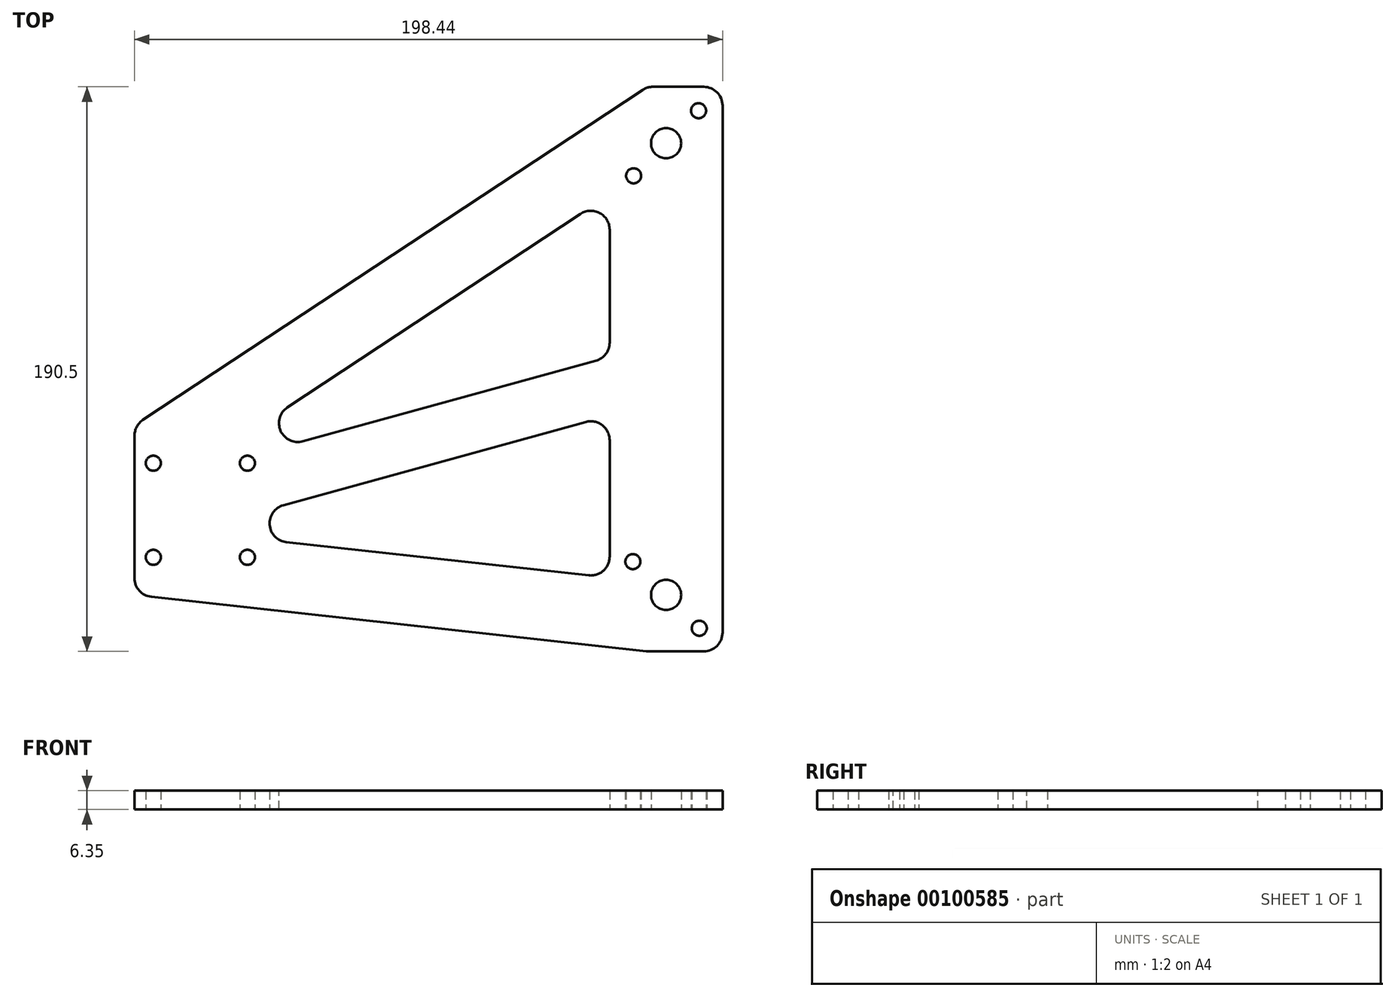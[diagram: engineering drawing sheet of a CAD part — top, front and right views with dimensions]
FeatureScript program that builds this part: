
annotation { "Feature Type Name" : "Feature", "Feature Type Description" : "" }
export const myFeature = defineFeature(function(context is Context, id is Id, definition is map)
    precondition{}
    {
        {
            var Q0;
            Q0=qCreatedBy(makeId("Top.planeOp"),FACE);
            var sketch = newSketch(context, id + "F0", { "sketchPlane" : qUnion([Q0])});
            skLineSegment(sketch, "E0.bottom", {"start": v(99.22, 127) * mm, "end": v(-99.22, 127) * mm});
            skLineSegment(sketch, "E0.top", {"start": v(99.22, -63.5) * mm, "end": v(-99.22, -63.5) * mm});
            skLineSegment(sketch, "E0.left", {"start": v(99.22, 127) * mm, "end": v(99.22, -63.5) * mm});
            skLineSegment(sketch, "E0.right", {"start": v(-99.22, 127) * mm, "end": v(-99.22, -63.5) * mm});
            skPoint(sketch, "E0.middle", {"position": v(0, 31.75) * mm});
            skPoint(sketch, "E1", {"position": v(80.17, 107.95) * mm});
            skPoint(sketch, "E2", {"position": v(80.17, -44.45) * mm});
            skPoint(sketch, "E3", {"position": v(-61.12, 0) * mm});
            skPoint(sketch, "E4", {"position": v(-92.87, 0) * mm});
            skPoint(sketch, "E5", {"position": v(-92.87, -31.75) * mm});
            skPoint(sketch, "E6", {"position": v(-61.12, -31.75) * mm});
            skLineSegment(sketch, "E7", {"start": v(73.82, 127) * mm, "end": v(-99.22, 12.7) * mm});
            skLineSegment(sketch, "E8", {"start": v(-99.22, -44.45) * mm, "end": v(73.82, -63.5) * mm});
            skPoint(sketch, "E9", {"position": v(91.14, 118.92) * mm});
            skPoint(sketch, "E10", {"position": v(69.2, 96.98) * mm});
            skLineSegment(sketch, "E11", {"start": v(69.2, 96.98) * mm, "end": v(91.14, 118.92) * mm});
            skLineSegment(sketch, "E12", {"start": v(68.94, -33.22) * mm, "end": v(91.4, -55.68) * mm});
            skPoint(sketch, "E13", {"position": v(68.94, -33.22) * mm});
            skPoint(sketch, "E14", {"position": v(91.4, -55.68) * mm});
            skLineSegment(sketch, "E15", {"start": v(-106.6, -20.15) * mm, "end": v(61.12, 90.63) * mm});
            skLineSegment(sketch, "E16", {"start": v(61.12, 90.63) * mm, "end": v(61.12, 35.89) * mm});
            skLineSegment(sketch, "E17", {"start": v(61.12, -38.62) * mm, "end": v(-106.6, -20.15) * mm});
            skLineSegment(sketch, "E18", {"start": v(-106.6, -20.15) * mm, "end": v(-119.46, -0.67) * mm});
            skLineSegment(sketch, "E19", {"start": v(-106.6, -20.15) * mm, "end": v(-109.15, -43.36) * mm});
            skLineSegment(sketch, "E20", {"start": v(61.12, 35.89) * mm, "end": v(-80.96, -3.22) * mm});
            skLineSegment(sketch, "E21", {"start": v(61.12, 16.13) * mm, "end": v(-80.96, -22.97) * mm});
            skLineSegment(sketch, "E22.trimOffspring", {"start": v(61.12, 16.13) * mm, "end": v(61.12, -38.62) * mm});
            skSolve(sketch);
        }
        {
            var Q0;
            {var subQ3=sQuery(id+"F0.wireOp",EDGE,"E0.left");Q0=makeQuery(id+"F0.imprint","IMPRINT",FACE,{"disambiguationData":[TD([[makeQuery(id+"F0.imprint","IMPRINT",EDGE,{"derivedFrom":subQ3}),-1.0]])]});}
            var Q1;
            {var subQ0=sQuery(id+"F0.wireOp",EDGE,"E18");Q1=makeQuery(id+"F0.imprint","IMPRINT",FACE,{"disambiguationData":[TD([[makeQuery(id+"F0.imprint","IMPRINT",EDGE,{"derivedFrom":subQ0}),1.0]])]});}
            extrude(context, id + "F1", {"entities" : qUnion([Q0, Q1]), "depth" : 6.35 * mm});
        }
        {
            var Q0;
            Q0=makeQuery(id+"F1.opExtrude","SWEPT_EDGE",EDGE,{"disambiguationData":[OSD([sQuery(id+"F0.wireOp",EDGE,"E0.bottom"),sQuery(id+"F0.wireOp",EDGE,"mwRxRHgS-zIiz-PPDk-q2ss-A3RoKZUUVuR5")])]});
            var Q1;
            Q1=makeQuery(id+"F1.opExtrude","SWEPT_EDGE",EDGE,{"disambiguationData":[OSD([sQuery(id+"F0.wireOp",EDGE,"E0.right"),sQuery(id+"F0.wireOp",EDGE,"mwRxRHgS-zIiz-PPDk-q2ss-A3RoKZUUVuR5")])]});
            var Q2;
            Q2=makeQuery(id+"F1.opExtrude","SWEPT_EDGE",EDGE,{"disambiguationData":[OSD([sQuery(id+"F0.wireOp",EDGE,"E0.right"),sQuery(id+"F0.wireOp",EDGE,"da7c650e-1eb5-4def-85a6-90974a040efa0.MirrorCS")])]});
            var Q3;
            Q3=makeQuery(id+"F1.opExtrude","SWEPT_EDGE",EDGE,{"disambiguationData":[OSD([sQuery(id+"F0.wireOp",EDGE,"E0.top"),sQuery(id+"F0.wireOp",EDGE,"da7c650e-1eb5-4def-85a6-90974a040efa0.MirrorCS")])]});
            var Q4;
            Q4=makeQuery(id+"F1.opExtrude","SWEPT_EDGE",EDGE,{"disambiguationData":[OSD([sQuery(id+"F0.wireOp",EDGE,"E0.top"),sQuery(id+"F0.wireOp",EDGE,"E0.left")])]});
            var Q5;
            Q5=makeQuery(id+"F1.opExtrude","SWEPT_EDGE",EDGE,{"disambiguationData":[OSD([sQuery(id+"F0.wireOp",EDGE,"E0.bottom"),sQuery(id+"F0.wireOp",EDGE,"E0.left")])]});
            var Q6;
            Q6=makeQuery(id+"F1.opExtrude","SWEPT_EDGE",EDGE,{"disambiguationData":[OSD([sQuery(id+"F0.wireOp",EDGE,"E15"),sQuery(id+"F0.wireOp",EDGE,"E20")])]});
            var Q7;
            Q7=makeQuery(id+"F1.opExtrude","SWEPT_EDGE",EDGE,{"disambiguationData":[OSD([sQuery(id+"F0.wireOp",EDGE,"E17"),sQuery(id+"F0.wireOp",EDGE,"E21")])]});
            var Q8;
            Q8=makeQuery(id+"F1.opExtrude","SWEPT_EDGE",EDGE,{"disambiguationData":[OSD([sQuery(id+"F0.wireOp",EDGE,"E15"),sQuery(id+"F0.wireOp",EDGE,"E16")])]});
            var Q9;
            Q9=makeQuery(id+"F1.opExtrude","SWEPT_EDGE",EDGE,{"disambiguationData":[OSD([sQuery(id+"F0.wireOp",EDGE,"E21"),sQuery(id+"F0.wireOp",EDGE,"E22.trimOffspring")])]});
            var Q10;
            Q10=makeQuery(id+"F1.opExtrude","SWEPT_EDGE",EDGE,{"disambiguationData":[OSD([sQuery(id+"F0.wireOp",EDGE,"E17"),sQuery(id+"F0.wireOp",EDGE,"E22.trimOffspring")])]});
            var Q11;
            Q11=makeQuery(id+"F1.opExtrude","SWEPT_EDGE",EDGE,{"disambiguationData":[OSD([sQuery(id+"F0.wireOp",EDGE,"E16"),sQuery(id+"F0.wireOp",EDGE,"E20")])]});
            fillet(context, id + "F2", {"entities" : qUnion([Q0, Q1, Q2, Q3, Q4, Q5, Q6, Q7, Q8, Q9, Q10, Q11]), "radius" : 6.35 * mm, "tangentPropagation" : true, "allowEdgeOverflow" : false});
        }
        {
            var Q0;
            Q0=sQuery(id+"F0.wireOp",VERTEX,"E1");
            var Q1;
            Q1=sQuery(id+"F0.wireOp",VERTEX,"E2");
            var Q2;
            Q2=makeQuery(id+"F1.opExtrude","SWEPT_BODY",BODY,{"disambiguationData":[OSD([sQuery(id+"F0.wireOp",EDGE,"E0.bottom"),sQuery(id+"F0.wireOp",EDGE,"E0.top"),sQuery(id+"F0.wireOp",EDGE,"E0.left"),sQuery(id+"F0.wireOp",EDGE,"E0.right"),sQuery(id+"F0.wireOp",EDGE,"E7"),sQuery(id+"F0.wireOp",EDGE,"E8")])]});
            hole(context, id + "F3", {"style" : HoleStyle.SIMPLE, "endStyle" : HoleEndStyle.THROUGH, "oppositeDirection" : true, "holeDiameter" : 10.16 * mm, "locations" : qUnion([Q0, Q1]), "scope" : qUnion([Q2]), "isTappedThrough" : true});
        }
        {
            var Q0;
            Q0=sQuery(id+"F0.wireOp",VERTEX,"E9");
            var Q1;
            Q1=sQuery(id+"F0.wireOp",VERTEX,"E10");
            var Q2;
            Q2=sQuery(id+"F0.wireOp",VERTEX,"E14");
            var Q3;
            Q3=sQuery(id+"F0.wireOp",VERTEX,"E13");
            var Q4;
            Q4=sQuery(id+"F0.wireOp",VERTEX,"E6");
            var Q5;
            Q5=sQuery(id+"F0.wireOp",VERTEX,"E4");
            var Q6;
            Q6=sQuery(id+"F0.wireOp",VERTEX,"E3");
            var Q7;
            Q7=sQuery(id+"F0.wireOp",VERTEX,"E5");
            var Q8;
            Q8=makeQuery(id+"F1.opExtrude","SWEPT_BODY",BODY,{"disambiguationData":[OSD([sQuery(id+"F0.wireOp",EDGE,"E0.bottom"),sQuery(id+"F0.wireOp",EDGE,"E0.top"),sQuery(id+"F0.wireOp",EDGE,"E0.left"),sQuery(id+"F0.wireOp",EDGE,"E0.right"),sQuery(id+"F0.wireOp",EDGE,"E7"),sQuery(id+"F0.wireOp",EDGE,"E8")])]});
            hole(context, id + "F4", {"style" : HoleStyle.SIMPLE, "endStyle" : HoleEndStyle.THROUGH, "oppositeDirection" : true, "holeDiameter" : 5.08 * mm, "locations" : qUnion([Q0, Q1, Q2, Q3, Q4, Q5, Q6, Q7]), "scope" : qUnion([Q8]), "isTappedThrough" : true});
        }
    });
